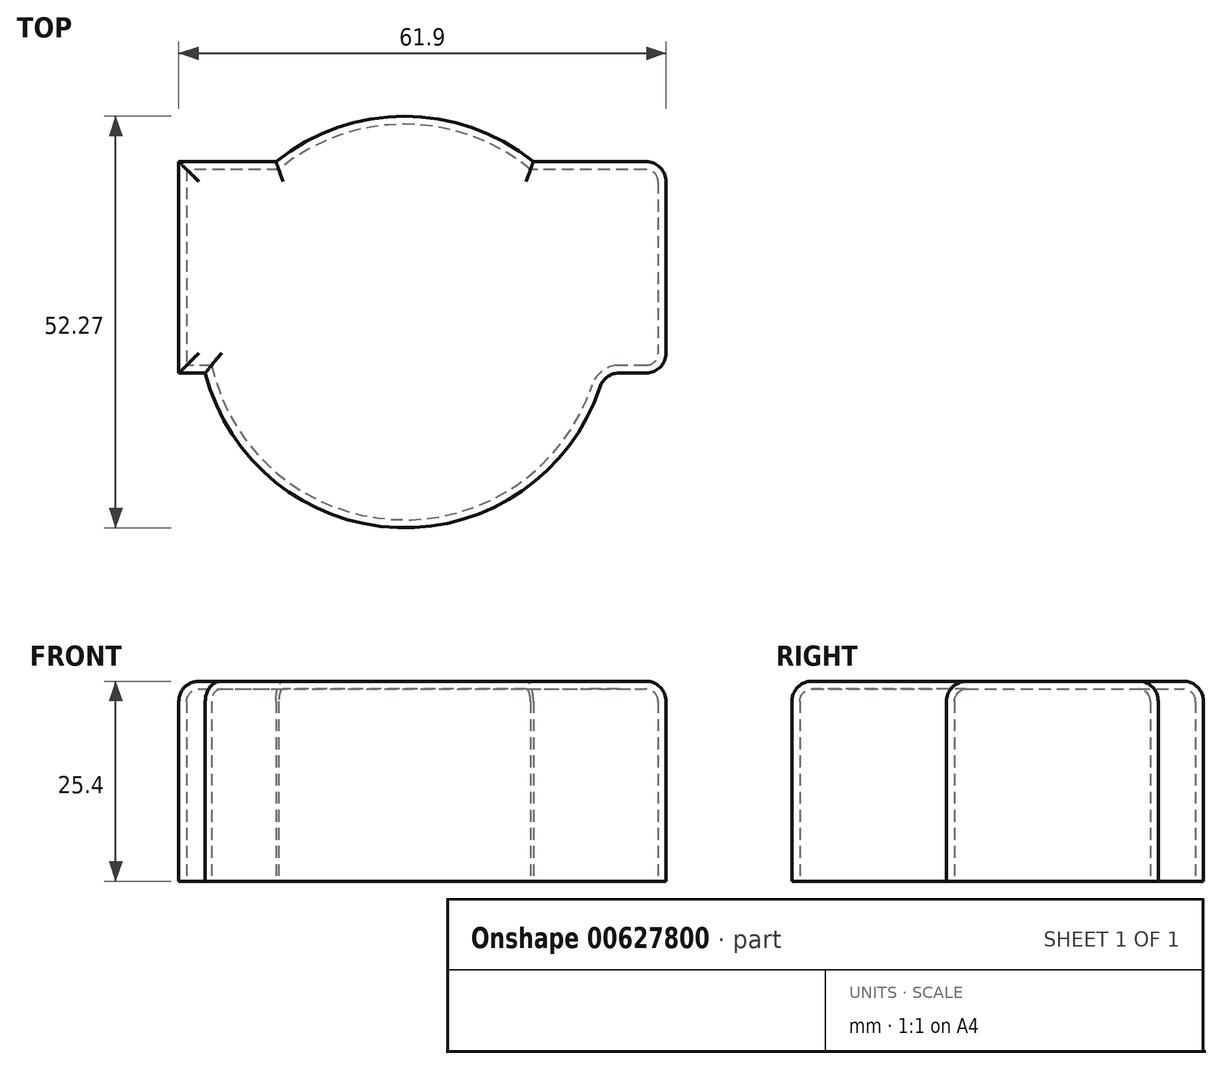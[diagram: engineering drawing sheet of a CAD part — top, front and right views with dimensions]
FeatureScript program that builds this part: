
annotation { "Feature Type Name" : "Feature", "Feature Type Description" : "" }
export const myFeature = defineFeature(function(context is Context, id is Id, definition is map)
    precondition{}
    {
        {
            var Q0;
            Q0=qCreatedBy(makeId("Top.planeOp"),FACE);
            var sketch = newSketch(context, id + "F0", { "sketchPlane" : qUnion([Q0])});
            skLineSegment(sketch, "E0.bottom", {"start": v(27.25, 41.68) * mm, "end": v(10.4, 41.68) * mm});
            skLineSegment(sketch, "E0.top", {"start": v(27.25, 14.8) * mm, "end": v(19.36, 14.8) * mm});
            skLineSegment(sketch, "E0.left", {"start": v(27.25, 41.68) * mm, "end": v(27.25, 14.8) * mm});
            skLineSegment(sketch, "E0.right", {"start": v(-34.65, 41.68) * mm, "end": v(-34.65, 14.8) * mm});
            skArc(sketch, "E1", {"start": v(10.4, 41.68) * mm, "mid": v(-5.95, 47.43) * mm, "end": v(-22.3, 41.68) * mm});
            skArc(sketch, "E2.trimOffspring", {"start": v(-31.27, 14.8) * mm, "mid": v(-5.95, -4.84) * mm, "end": v(19.36, 14.8) * mm});
            skLineSegment(sketch, "E3.trimOffspring", {"start": v(-22.3, 41.68) * mm, "end": v(-34.65, 41.68) * mm});
            skLineSegment(sketch, "E4.trimOffspring", {"start": v(-31.27, 14.8) * mm, "end": v(-34.65, 14.8) * mm});
            skSolve(sketch);
        }
        {
            var Q0;
            Q0 = qSketchRegion(id + "F0", true);
            extrude(context, id + "F1", {"entities" : qUnion([Q0]), "depth" : 25.4 * mm, "offsetDistance" : 25.4 * mm});
        }
        {
            var Q0;
            Q0=makeQuery(id+"F1.opExtrude","CAP_EDGE",EDGE,{"disambiguationData":[OSD([sQuery(id+"F0.wireOp",EDGE,"E0.left")])],"isStart":false});
            var Q1;
            Q1=makeQuery(id+"F1.opExtrude","CAP_EDGE",EDGE,{"disambiguationData":[OSD([sQuery(id+"F0.wireOp",EDGE,"E2.trimOffspring")])],"isStart":false});
            var Q2;
            Q2=makeQuery(id+"F1.opExtrude","CAP_EDGE",EDGE,{"disambiguationData":[OSD([sQuery(id+"F0.wireOp",EDGE,"E0.top")])],"isStart":false});
            var Q3;
            Q3=makeQuery(id+"F1.opExtrude","CAP_EDGE",EDGE,{"disambiguationData":[OSD([sQuery(id+"F0.wireOp",EDGE,"E0.bottom")])],"isStart":false});
            var Q4;
            Q4=makeQuery(id+"F1.opExtrude","CAP_EDGE",EDGE,{"disambiguationData":[OSD([sQuery(id+"F0.wireOp",EDGE,"E1")])],"isStart":false});
            var Q5;
            Q5=makeQuery(id+"F1.opExtrude","CAP_EDGE",EDGE,{"disambiguationData":[OSD([sQuery(id+"F0.wireOp",EDGE,"E3.trimOffspring")])],"isStart":false});
            var Q6;
            Q6=makeQuery(id+"F1.opExtrude","CAP_EDGE",EDGE,{"disambiguationData":[OSD([sQuery(id+"F0.wireOp",EDGE,"E0.right")])],"isStart":false});
            var Q7;
            Q7=makeQuery(id+"F1.opExtrude","CAP_EDGE",EDGE,{"disambiguationData":[OSD([sQuery(id+"F0.wireOp",EDGE,"E4.trimOffspring")])],"isStart":false});
            var Q8;
            Q8=makeQuery(id+"F1.opExtrude","SWEPT_EDGE",EDGE,{"disambiguationData":[OSD([sQuery(id+"F0.wireOp",EDGE,"E0.bottom"),sQuery(id+"F0.wireOp",EDGE,"E0.left")])]});
            var Q9;
            Q9=makeQuery(id+"F1.opExtrude","SWEPT_EDGE",EDGE,{"disambiguationData":[OSD([sQuery(id+"F0.wireOp",EDGE,"E0.top"),sQuery(id+"F0.wireOp",EDGE,"E0.left")])]});
            var Q10;
            Q10=makeQuery(id+"F1.opExtrude","SWEPT_EDGE",EDGE,{"disambiguationData":[OSD([sQuery(id+"F0.wireOp",EDGE,"E0.top"),sQuery(id+"F0.wireOp",EDGE,"E2.trimOffspring")])]});
            fillet(context, id + "F2", {"entities" : qUnion([Q0, Q1, Q2, Q3, Q4, Q5, Q6, Q7, Q8, Q9, Q10]), "radius" : 2.54 * mm, "tangentPropagation" : true, "allowEdgeOverflow" : false});
        }
        {
            var Q0;
            Q0=makeQuery(id+"F1.opExtrude","CAP_FACE",FACE,{"disambiguationData":[OSD([sQuery(id+"F0.wireOp",EDGE,"E0.bottom"),sQuery(id+"F0.wireOp",EDGE,"E0.top"),sQuery(id+"F0.wireOp",EDGE,"E0.left"),sQuery(id+"F0.wireOp",EDGE,"E0.right"),sQuery(id+"F0.wireOp",EDGE,"E1"),sQuery(id+"F0.wireOp",EDGE,"E2.trimOffspring"),sQuery(id+"F0.wireOp",EDGE,"E3.trimOffspring"),sQuery(id+"F0.wireOp",EDGE,"E4.trimOffspring")])],"isStart":true});
            shell(context, id + "F3", {"entities" : qUnion([Q0]), "thickness" : 1 * mm});
        }
    });
